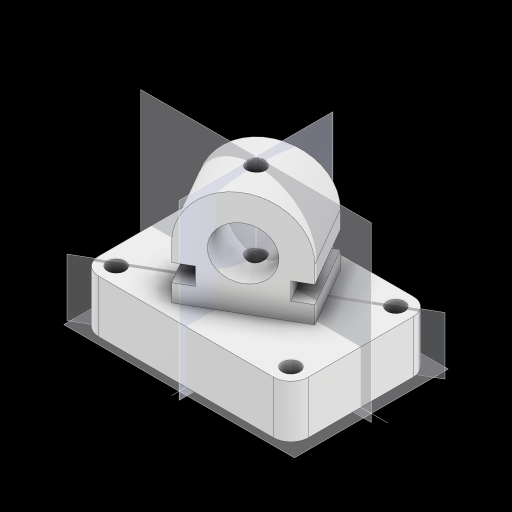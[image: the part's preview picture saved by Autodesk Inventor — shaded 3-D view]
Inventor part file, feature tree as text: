
AUTODESK INVENTOR PART (.ipt)
format: ipt  version: 2024 (Build 280153000, 153)  size: 210,944 bytes
history: native  units: in
note: dims shown in document units (in); Inventor stores cm internally (conversion verified against a paired STEP export)
features: sketch x3, extrude x2, hole x1
ambient origin geometry x8: Origin, YZ Plane, XZ Plane, XY Plane, X Axis, Y Axis, Z Axis, Center Point
bodies: Solid1 (feature_tree)
feature tree (6):
  extrude  "MAIN BODY"  Depth=0.25in
  extrude  "TOP BOSS"  Depth=2.0in
  hole  "THROUGH HOLE"  [1 undecoded]
  sketch  "Sketch1"  dims[d0=0.25in d1=0.25in]
  sketch  "Sketch2"  dims[d2=3.0in d3=2.0in]
  sketch  "Sketch6"  dims[d4=1.5in d5=1.0in d6=0.75in d7=0.0in d8=30.0deg d9=0.75in d10=0.25in d11=0.25in d13=0.25in d14=0.25in d15=1.5in d17=0.75in d18=0.25in d19=0.25in d20=0.75in d21=1.0in d22=0.0in d67=0.25in d68=0.75in d69=0.375in d70=0.25in d71=0.5635in d72=1.0in d73=0.8108in d74=0.75in d75=0.8108in d76=0.0625in d77=0.75in d78=0.375in]
note: 1 required parameter value undecoded (feature->parameter linkage not recoverable at this tier; creation-order binding heuristic only, values carry confidence <= 0.55)
